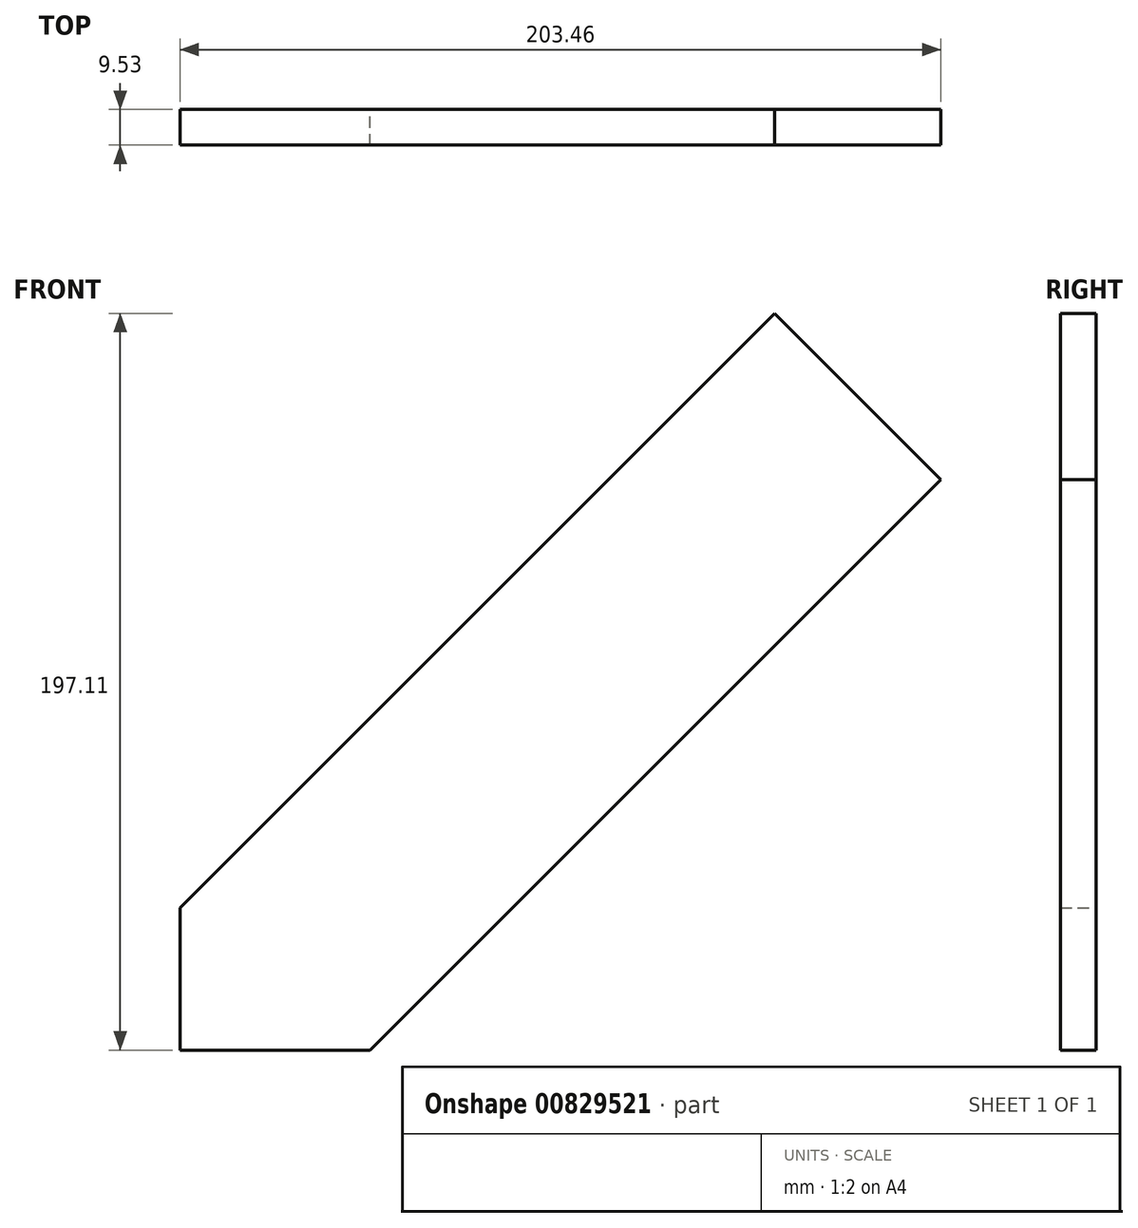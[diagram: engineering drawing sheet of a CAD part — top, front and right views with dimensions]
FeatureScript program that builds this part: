
annotation { "Feature Type Name" : "Feature", "Feature Type Description" : "" }
export const myFeature = defineFeature(function(context is Context, id is Id, definition is map)
    precondition{}
    {
        {
            var Q0;
            Q0=qCreatedBy(makeId("Front.planeOp"),FACE);
            var sketch = newSketch(context, id + "F0", { "sketchPlane" : qUnion([Q0])});
            skLineSegment(sketch, "E0", {"start": v(-155.62, 0) * mm, "end": v(-104.82, 0) * mm});
            skLineSegment(sketch, "E1", {"start": v(-104.82, 0) * mm, "end": v(47.84, 152.66) * mm});
            skLineSegment(sketch, "E2", {"start": v(47.84, 152.66) * mm, "end": v(3.4, 197.11) * mm});
            skLineSegment(sketch, "E3", {"start": v(3.4, 197.11) * mm, "end": v(-155.62, 38.1) * mm});
            skLineSegment(sketch, "E4", {"start": v(-155.62, 38.1) * mm, "end": v(-155.62, 0) * mm});
            skSolve(sketch);
        }
        {
            var Q0;
            Q0 = qSketchRegion(id + "F0", true);
            extrude(context, id + "F1", {"entities" : qUnion([Q0]), "depth" : 9.52 * mm, "offsetDistance" : 25.4 * mm});
        }
    });
